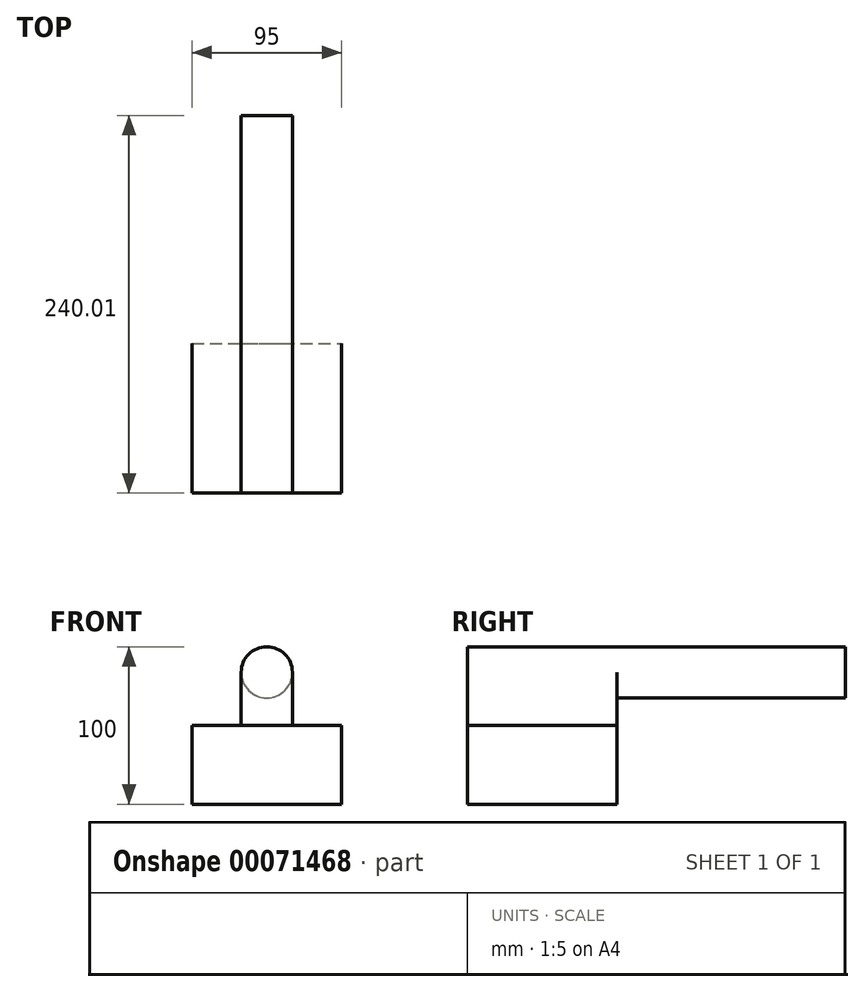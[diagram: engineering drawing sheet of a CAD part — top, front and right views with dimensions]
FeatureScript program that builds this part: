
annotation { "Feature Type Name" : "Feature", "Feature Type Description" : "" }
export const myFeature = defineFeature(function(context is Context, id is Id, definition is map)
    precondition{}
    {
        {
            var Q0;
            Q0=qCreatedBy(makeId("Front.planeOp"),FACE);
            var sketch = newSketch(context, id + "F0", { "sketchPlane" : qUnion([Q0])});
            skLineSegment(sketch, "E0.bottom", {"start": v(-44.75, 7.2) * mm, "end": v(50.25, 7.2) * mm});
            skLineSegment(sketch, "E0.top", {"start": v(-44.75, -42.78) * mm, "end": v(50.25, -42.78) * mm});
            skLineSegment(sketch, "E0.left", {"start": v(-44.75, 7.2) * mm, "end": v(-44.75, -42.78) * mm});
            skLineSegment(sketch, "E0.right", {"start": v(50.25, 7.2) * mm, "end": v(50.25, -42.78) * mm});
            skSolve(sketch);
        }
        {
            var Q0;
            Q0 = qSketchRegion(id + "F0", true);
            extrude(context, id + "F1", {"entities" : qUnion([Q0]), "depth" : 95 * mm});
        }
        {
            var Q0;
            Q0=makeQuery(id+"F1.opExtrude","CAP_FACE",FACE,{"disambiguationData":[OSD([sQuery(id+"F0.wireOp",EDGE,"E0.bottom"),sQuery(id+"F0.wireOp",EDGE,"E0.top"),sQuery(id+"F0.wireOp",EDGE,"E0.left"),sQuery(id+"F0.wireOp",EDGE,"E0.right")])],"isStart":false});
            var sketch = newSketch(context, id + "F2", { "sketchPlane" : qUnion([Q0])});
            skLineSegment(sketch, "E1.bottom", {"start": v(-13.5, 7.2) * mm, "end": v(19, 7.2) * mm});
            skLineSegment(sketch, "E1.top", {"start": v(-13.5, 24.7) * mm, "end": v(19, 24.7) * mm});
            skLineSegment(sketch, "E1.left", {"start": v(-13.5, 7.2) * mm, "end": v(-13.5, 24.7) * mm});
            skLineSegment(sketch, "E1.right", {"start": v(19, 7.2) * mm, "end": v(19, 24.7) * mm});
            skSolve(sketch);
        }
        {
            var Q0;
            Q0 = qSketchRegion(id + "F2", true);
            extrude(context, id + "F3", {"entities" : qUnion([Q0]), "oppositeDirection" : true, "depth" : 95 * mm});
        }
        {
            var Q0;
            Q0=makeQuery(id+"F3.opExtrude","CAP_FACE",FACE,{"disambiguationData":[OSD([sQuery(id+"F2.wireOp",EDGE,"E1.bottom"),sQuery(id+"F2.wireOp",EDGE,"E1.top"),sQuery(id+"F2.wireOp",EDGE,"E1.left"),sQuery(id+"F2.wireOp",EDGE,"E1.right")])],"isStart":true});
            var sketch = newSketch(context, id + "F4", { "sketchPlane" : qUnion([Q0])});
            skCircle(sketch, "E2", {"center": v(2.75, 40.96) * mm, "radius": 16.26 * mm});
            skPoint(sketch, "E2.centerSnap0", {"position": v(2.75, 24.7) * mm});
            skSolve(sketch);
        }
        {
            var Q0;
            Q0 = qSketchRegion(id + "F4", true);
            extrude(context, id + "F5", {"entities" : qUnion([Q0]), "oppositeDirection" : true, "depth" : 240 * mm});
        }
        {
            var Q0;
            Q0=makeQuery(id+"F3.opExtrude","CAP_FACE",FACE,{"disambiguationData":[OSD([sQuery(id+"F2.wireOp",EDGE,"E1.bottom"),sQuery(id+"F2.wireOp",EDGE,"E1.top"),sQuery(id+"F2.wireOp",EDGE,"E1.left"),sQuery(id+"F2.wireOp",EDGE,"E1.right")])],"isStart":true});
            var sketch = newSketch(context, id + "F6", { "sketchPlane" : qUnion([Q0])});
            skLineSegment(sketch, "E3.bottom", {"start": v(-13.5, 24.7) * mm, "end": v(19, 24.7) * mm});
            skLineSegment(sketch, "E3.top", {"start": v(-13.5, 40.96) * mm, "end": v(19, 40.96) * mm});
            skLineSegment(sketch, "E3.left", {"start": v(-13.5, 24.7) * mm, "end": v(-13.5, 40.96) * mm});
            skLineSegment(sketch, "E3.right", {"start": v(19, 24.7) * mm, "end": v(19, 40.96) * mm});
            skSolve(sketch);
        }
        {
            var Q0;
            Q0 = qSketchRegion(id + "F6", true);
            extrude(context, id + "F7", {"entities" : qUnion([Q0]), "operationType" : NewBodyOperationType.ADD, "oppositeDirection" : true, "depth" : 95 * mm});
        }
    });
